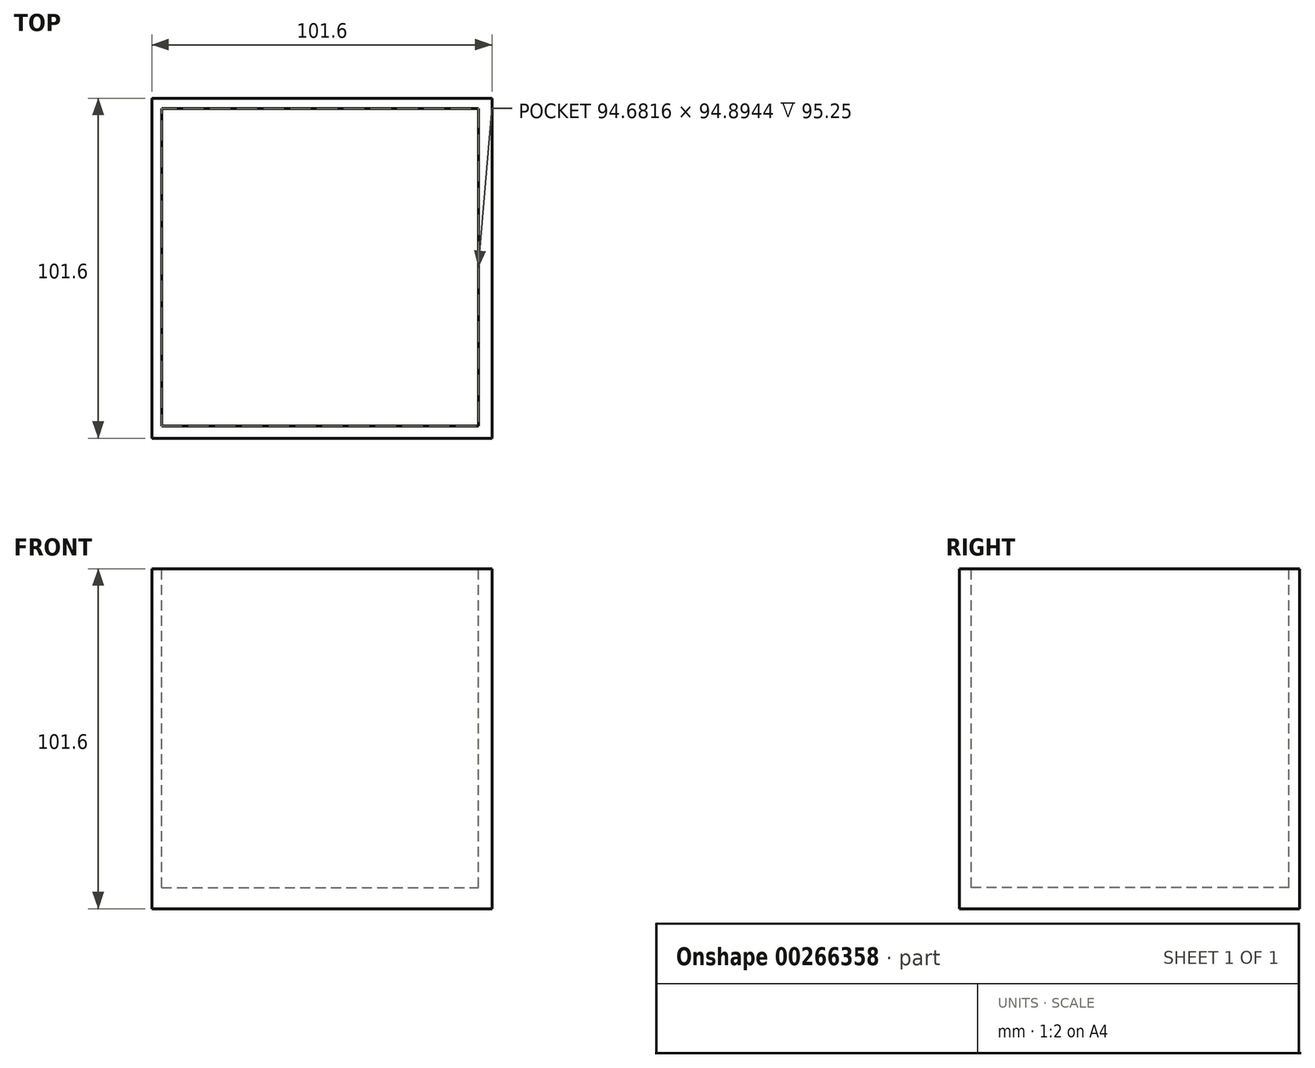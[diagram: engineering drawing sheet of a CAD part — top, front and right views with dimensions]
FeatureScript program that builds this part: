
annotation { "Feature Type Name" : "Feature", "Feature Type Description" : "" }
export const myFeature = defineFeature(function(context is Context, id is Id, definition is map)
    precondition{}
    {
        {
            var Q0;
            Q0=qCreatedBy(makeId("Front.planeOp"),FACE);
            var sketch = newSketch(context, id + "F0", { "sketchPlane" : qUnion([Q0])});
            skLineSegment(sketch, "E0.bottom", {"start": v(0, 0) * mm, "end": v(-101.6, 0) * mm});
            skLineSegment(sketch, "E0.top", {"start": v(0, 101.6) * mm, "end": v(-101.6, 101.6) * mm});
            skLineSegment(sketch, "E0.left", {"start": v(0, 0) * mm, "end": v(0, 101.6) * mm});
            skLineSegment(sketch, "E0.right", {"start": v(-101.6, 0) * mm, "end": v(-101.6, 101.6) * mm});
            skSolve(sketch);
        }
        {
            var Q0;
            Q0 = qSketchRegion(id + "F0", true);
            extrude(context, id + "F1", {"entities" : qUnion([Q0]), "depth" : 101.6 * mm});
        }
        {
            var Q0;
            Q0=makeQuery(id+"F1.opExtrude","SWEPT_FACE",FACE,{"disambiguationData":[OSD([sQuery(id+"F0.wireOp",EDGE,"E0.top")])]});
            var sketch = newSketch(context, id + "F2", { "sketchPlane" : qUnion([Q0])});
            skLineSegment(sketch, "E1.bottom", {"start": v(-98.65, -3.11) * mm, "end": v(-3.97, -3.11) * mm});
            skLineSegment(sketch, "E1.top", {"start": v(-98.65, -98) * mm, "end": v(-3.97, -98) * mm});
            skLineSegment(sketch, "E1.left", {"start": v(-98.65, -3.11) * mm, "end": v(-98.65, -98) * mm});
            skLineSegment(sketch, "E1.right", {"start": v(-3.97, -3.11) * mm, "end": v(-3.97, -98) * mm});
            skSolve(sketch);
        }
        {
            var Q0;
            Q0 = qSketchRegion(id + "F2", true);
            var Q1;
            Q1=makeQuery(id+"F1.opExtrude","SWEPT_FACE",FACE,{"disambiguationData":[OSD([sQuery(id+"F0.wireOp",EDGE,"E0.bottom")])]});
            extrude(context, id + "F3", {"entities" : qUnion([Q0, Q1]), "operationType" : NewBodyOperationType.REMOVE, "oppositeDirection" : true, "depth" : 95.25 * mm});
        }
    });
